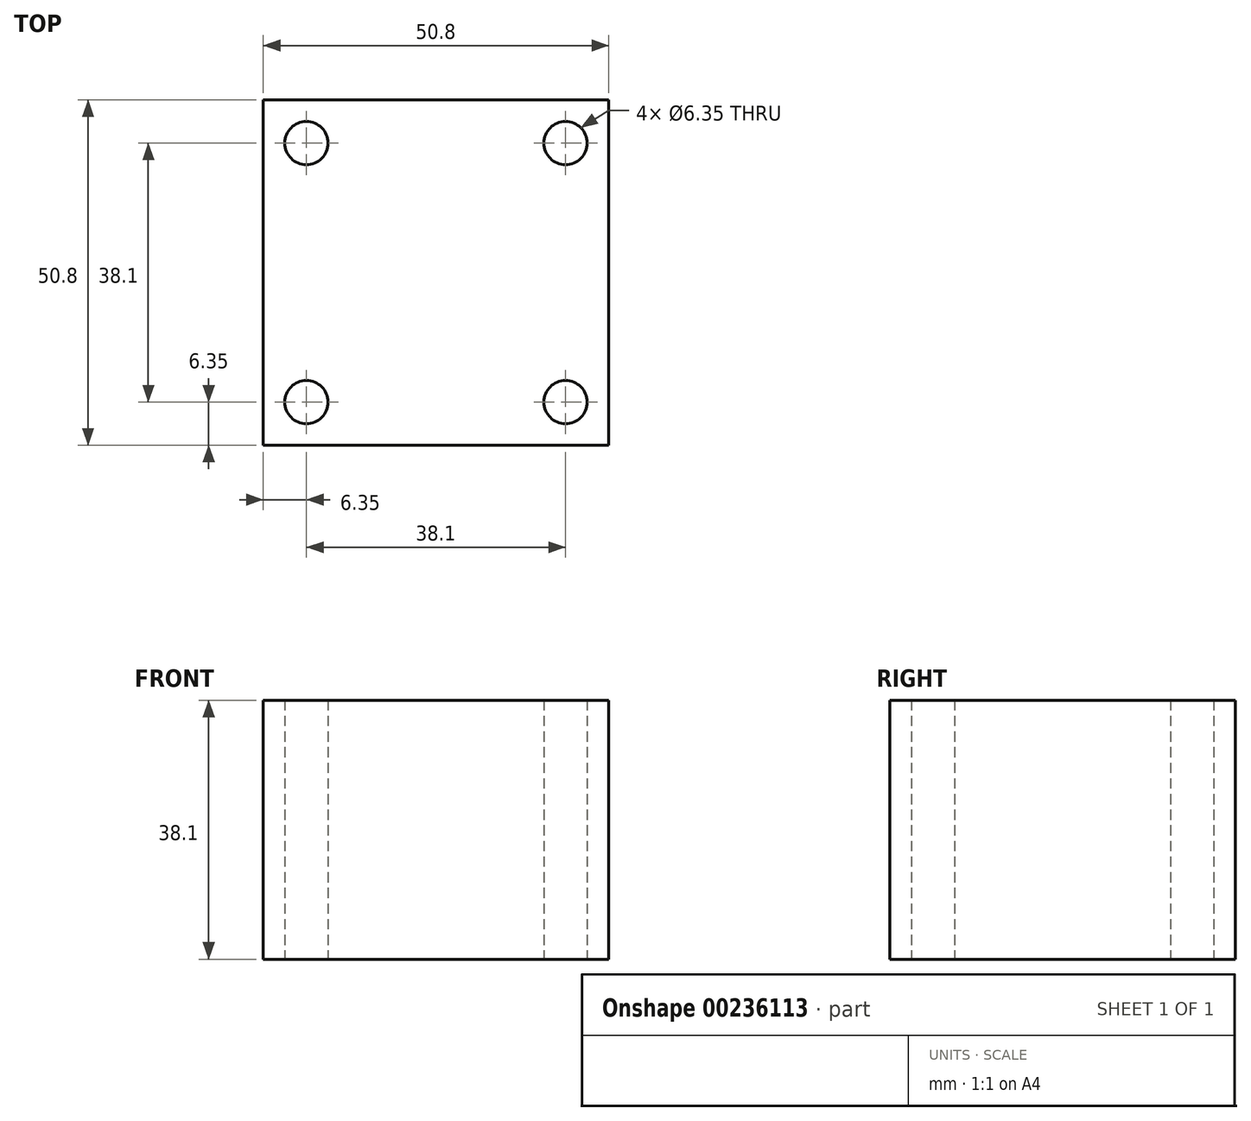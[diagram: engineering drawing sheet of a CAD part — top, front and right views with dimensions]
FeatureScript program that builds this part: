
annotation { "Feature Type Name" : "Feature", "Feature Type Description" : "" }
export const myFeature = defineFeature(function(context is Context, id is Id, definition is map)
    precondition{}
    {
        {
            var Q0;
            Q0=qCreatedBy(makeId("Top.planeOp"),FACE);
            var sketch = newSketch(context, id + "F0", { "sketchPlane" : qUnion([Q0])});
            skLineSegment(sketch, "E0.bottom", {"start": v(25.4, 25.4) * mm, "end": v(-25.4, 25.4) * mm});
            skLineSegment(sketch, "E0.top", {"start": v(25.4, -25.4) * mm, "end": v(-25.4, -25.4) * mm});
            skLineSegment(sketch, "E0.left", {"start": v(25.4, 25.4) * mm, "end": v(25.4, -25.4) * mm});
            skLineSegment(sketch, "E0.right", {"start": v(-25.4, 25.4) * mm, "end": v(-25.4, -25.4) * mm});
            skPoint(sketch, "E0.middle", {"position": v(0, 0) * mm});
            skCircle(sketch, "E1", {"center": v(-19.05, 19.05) * mm, "radius": 3.18 * mm});
            skCircle(sketch, "E2.MirrorC", {"center": v(19.05, 19.05) * mm, "radius": 3.18 * mm});
            skCircle(sketch, "E3.MirrorC", {"center": v(19.05, -19.05) * mm, "radius": 3.18 * mm});
            skCircle(sketch, "E4.MirrorC", {"center": v(-19.05, -19.05) * mm, "radius": 3.18 * mm});
            skSolve(sketch);
        }
        {
            var Q0;
            Q0 = qSketchRegion(id + "F0", true);
            extrude(context, id + "F1", {"entities" : qUnion([Q0]), "endBound" : BoundingType.SYMMETRIC, "depth" : 38.1 * mm});
        }
        {
            var Q0;
            Q0=qCreatedBy(makeId("Right.planeOp"),FACE);
            var sketch = newSketch(context, id + "F2", { "sketchPlane" : qUnion([Q0])});
            skCircle(sketch, "E5", {"center": v(0, -9.53) * mm, "radius": 6.35 * mm});
            skSolve(sketch);
        }
        {
            var Q0;
            Q0=sQuery(id+"F2.wireOp",EDGE,"E5");
            extrude(context, id + "F3", {"bodyType" : ToolBodyType.SURFACE, "surfaceEntities" : qUnion([Q0]), "endBound" : BoundingType.SYMMETRIC, "depth" : 152.4 * mm});
        }
    });
